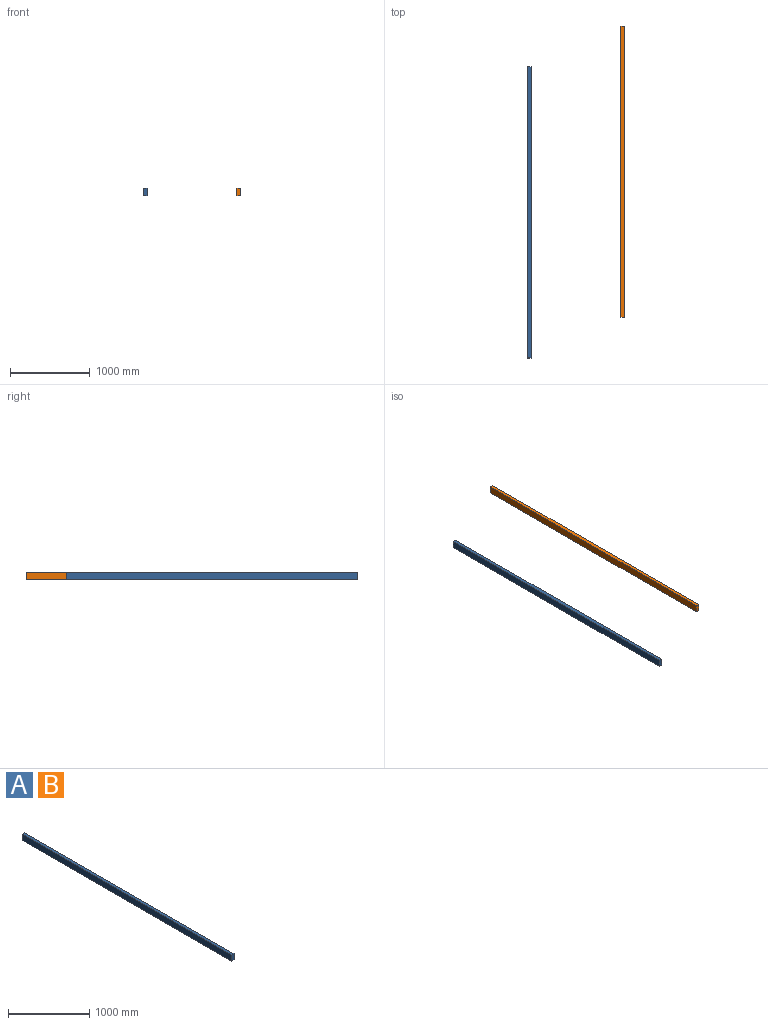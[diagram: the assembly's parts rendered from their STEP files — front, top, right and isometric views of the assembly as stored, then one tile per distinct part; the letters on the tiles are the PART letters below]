
ASSEMBLY  parts=2 mates=2
PART A: 6 faces, bbox 41.3x3657.6x92.1 mm
  f0: plane 3657.6x92.08mm, normal (-1,0,0), area 336773.5mm2, adj f1,f3,f4,f5
  f1: plane 92.08x41.28mm, normal (0,-1,0), area 3800.4mm2, adj f0,f2,f4,f5
  f2: plane 3657.6x92.08mm, normal (1,0,0), area 336773.5mm2, adj f1,f3,f4,f5
  f3: plane 92.08x41.28mm, normal (0,1,0), area 3800.4mm2, adj f0,f2,f4,f5
  f4: plane 3657.6x41.28mm, normal (0,0,-1), area 150967.4mm2, adj f0,f1,f2,f3
  f5: plane 3657.6x41.28mm, normal (0,0,1), area 150967.4mm2, adj f0,f1,f2,f3
PART B: same geometry as A
PLACE A rot(axis=(-1,0,0),0deg) t=(-532.76,-161.48,325.86)mm
PLACE B rot(axis=(-1,0,0),0deg) t=(638.19,350.74,325.86)mm
MATE parallel B.f0 <-> A.f2  axis (-1,0,0) through (596.29,355.07,279.82)mm
MATE parallel A.f5 <-> B.f5  axis (0,0,1) through (-554.02,-157.15,325.86)mm
